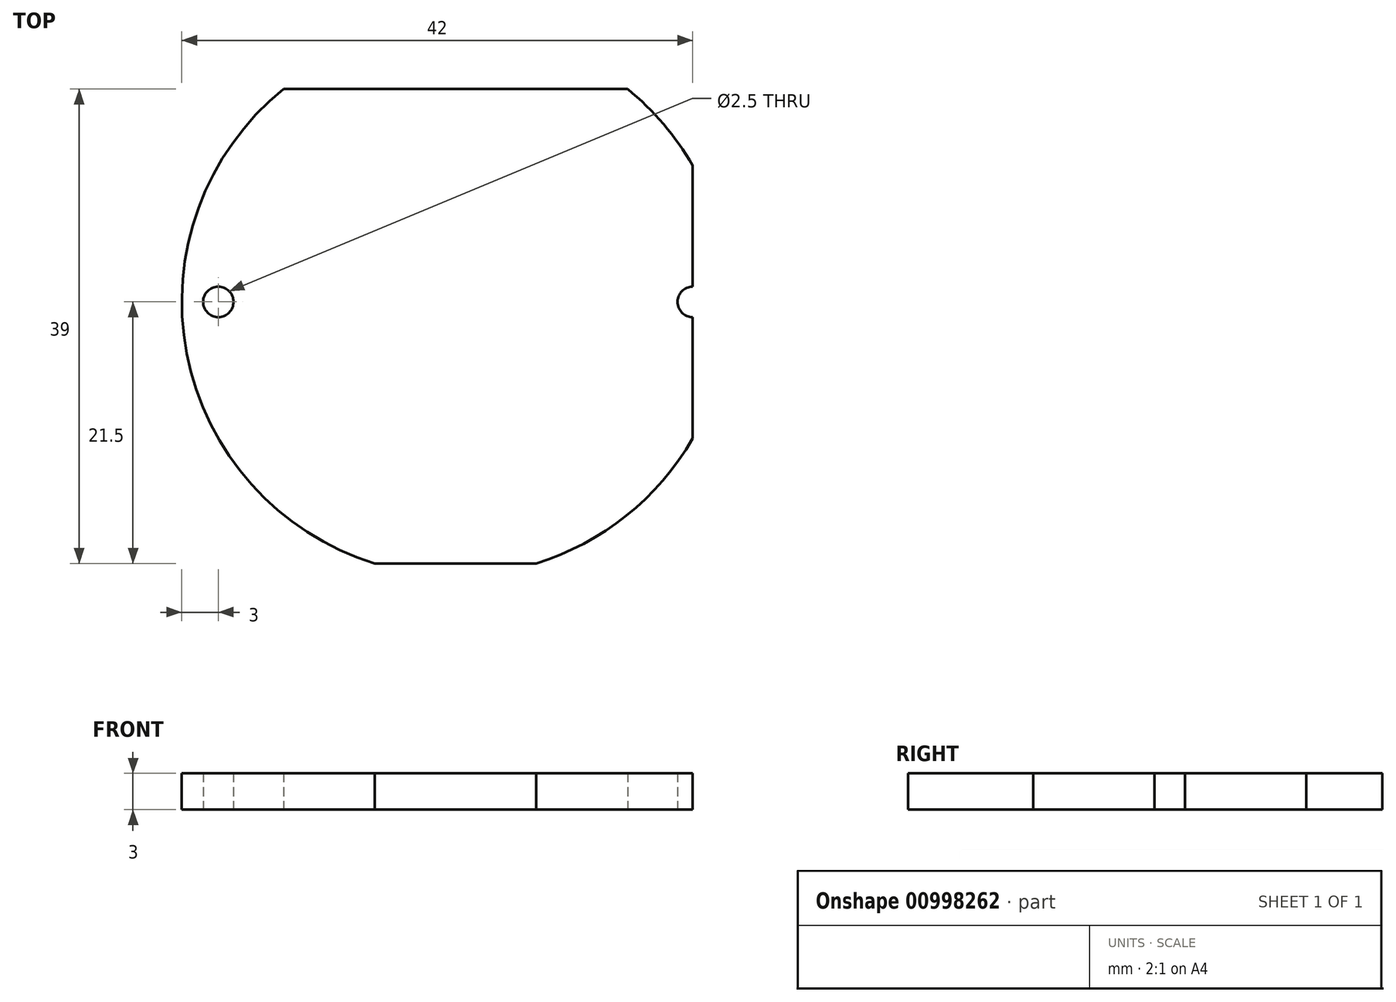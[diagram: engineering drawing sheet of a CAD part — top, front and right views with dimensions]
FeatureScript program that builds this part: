
annotation { "Feature Type Name" : "Feature", "Feature Type Description" : "" }
export const myFeature = defineFeature(function(context is Context, id is Id, definition is map)
    precondition{}
    {
        {
            var Q0;
            Q0=qCreatedBy(makeId("Top.planeOp"),FACE);
            var sketch = newSketch(context, id + "F0", { "sketchPlane" : qUnion([Q0])});
            skArc(sketch, "E0", {"start": v(-14.14, 17.5) * mm, "mid": v(0, -22.5) * mm, "end": v(14.14, 17.5) * mm});
            skLineSegment(sketch, "E1", {"start": v(-14.14, 17.5) * mm, "end": v(14.14, 17.5) * mm});
            skLineSegment(sketch, "E2", {"start": v(-17.2, 14.5) * mm, "end": v(17.2, 14.5) * mm});
            skLineSegment(sketch, "E3", {"start": v(-19.5, 11.22) * mm, "end": v(-19.5, -11.22) * mm});
            skLineSegment(sketch, "E4", {"start": v(19.5, -11.22) * mm, "end": v(19.5, 11.22) * mm});
            skCircle(sketch, "E5", {"center": v(-19.5, 0) * mm, "radius": 1.25 * mm});
            skCircle(sketch, "E6", {"center": v(19.5, 0) * mm, "radius": 1.25 * mm});
            skLineSegment(sketch, "E7", {"start": v(-6.63, -21.5) * mm, "end": v(6.63, -21.5) * mm});
            skSolve(sketch);
        }
        {
            var Q0;
            {var subQ0=sQuery(id+"F0.wireOp",EDGE,"E2");var subQ1=sQuery(id+"F0.wireOp",EDGE,"E0");var subQ2=makeQuery(id+"F0.imprint","INTERSECT",VERTEX,{"disambiguationData":[OD(0.0)],"derivedFrom":[subQ1,subQ0]});Q0=makeQuery(id+"F0.imprint","IMPRINT",FACE,{"disambiguationData":[TD([[makeQuery(id+"F0.imprint","IMPRINT",EDGE,{"disambiguationData":[TD([[subQ2,-1.0]])],"derivedFrom":subQ1}),1.0]])]});}
            var Q1;
            {var subQ0=sQuery(id+"F0.wireOp",EDGE,"E1");Q1=makeQuery(id+"F0.imprint","IMPRINT",FACE,{"disambiguationData":[TD([[makeQuery(id+"F0.imprint","IMPRINT",EDGE,{"derivedFrom":subQ0}),-1.0]])]});}
            var Q2;
            {var subQ0=sQuery(id+"F0.wireOp",EDGE,"E3");var subQ1=sQuery(id+"F0.wireOp",EDGE,"E0");var subQ2=makeQuery(id+"F0.imprint","INTERSECT",VERTEX,{"disambiguationData":[OD(0.0)],"derivedFrom":[subQ1,subQ0]});Q2=makeQuery(id+"F0.imprint","IMPRINT",FACE,{"disambiguationData":[TD([[makeQuery(id+"F0.imprint","IMPRINT",EDGE,{"disambiguationData":[TD([[subQ2,-1.0]])],"derivedFrom":subQ1}),1.0]])]});}
            var Q3;
            {var subQ0=sQuery(id+"F0.wireOp",EDGE,"E4");var subQ1=sQuery(id+"F0.wireOp",EDGE,"E0");var subQ2=makeQuery(id+"F0.imprint","INTERSECT",VERTEX,{"disambiguationData":[OD(0.0)],"derivedFrom":[subQ1,subQ0]});Q3=makeQuery(id+"F0.imprint","IMPRINT",FACE,{"disambiguationData":[TD([[makeQuery(id+"F0.imprint","IMPRINT",EDGE,{"disambiguationData":[TD([[subQ2,-1.0]])],"derivedFrom":subQ1}),1.0]])]});}
            extrude(context, id + "F1", {"entities" : qUnion([Q0, Q1, Q2, Q3]), "depth" : 3 * mm, "offsetDistance" : 25 * mm});
        }
    });
